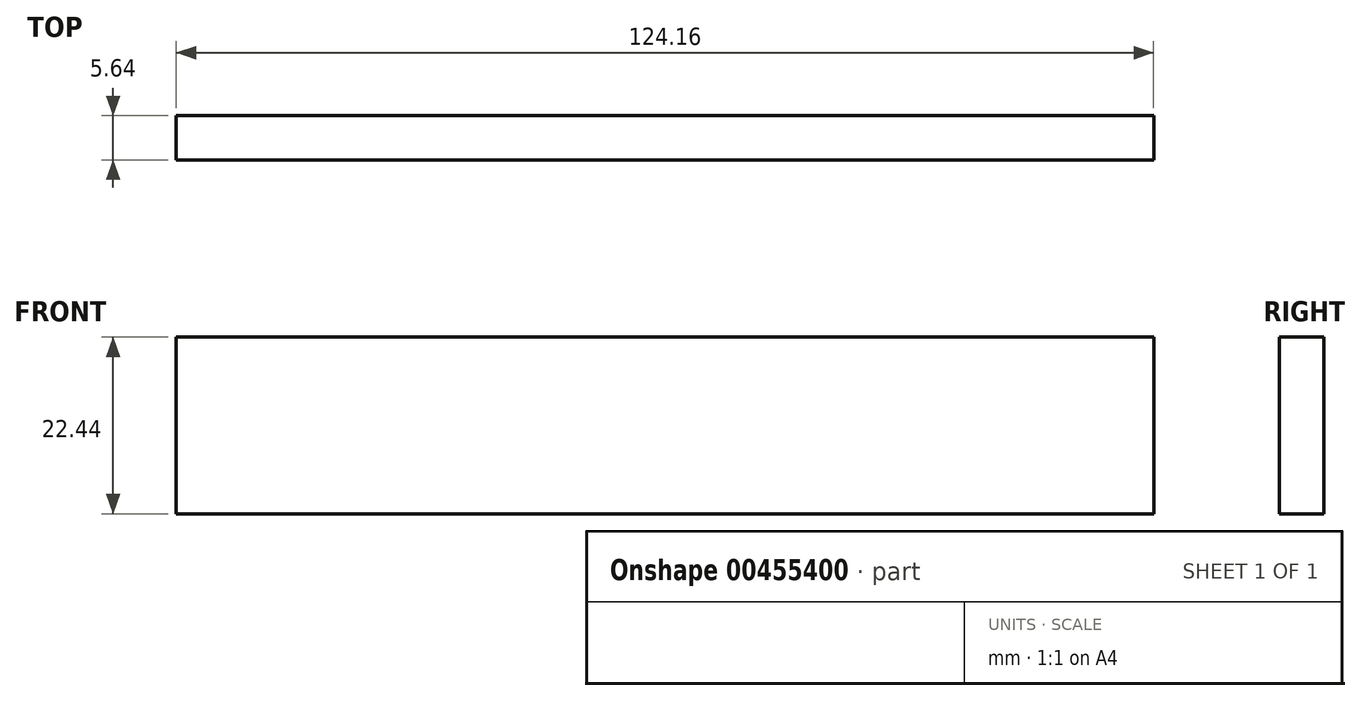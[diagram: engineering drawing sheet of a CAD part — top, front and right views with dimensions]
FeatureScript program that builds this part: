
annotation { "Feature Type Name" : "Feature", "Feature Type Description" : "" }
export const myFeature = defineFeature(function(context is Context, id is Id, definition is map)
    precondition{}
    {
        {
            var Q0;
            Q0=qCreatedBy(makeId("Front.planeOp"),FACE);
            var sketch = newSketch(context, id + "F0", { "sketchPlane" : qUnion([Q0])});
            skLineSegment(sketch, "E0.bottom", {"start": v(-62.08, 11.22) * mm, "end": v(62.08, 11.22) * mm});
            skLineSegment(sketch, "E0.top", {"start": v(-62.08, -11.22) * mm, "end": v(62.08, -11.22) * mm});
            skLineSegment(sketch, "E0.left", {"start": v(-62.08, 11.22) * mm, "end": v(-62.08, -11.22) * mm});
            skLineSegment(sketch, "E0.right", {"start": v(62.08, 11.22) * mm, "end": v(62.08, -11.22) * mm});
            skPoint(sketch, "E0.middle", {"position": v(0, 0) * mm});
            skSolve(sketch);
        }
        {
            var Q0;
            Q0 = qSketchRegion(id + "F0", true);
            extrude(context, id + "F1", {"entities" : qUnion([Q0]), "depth" : 5.64 * mm});
        }
    });
